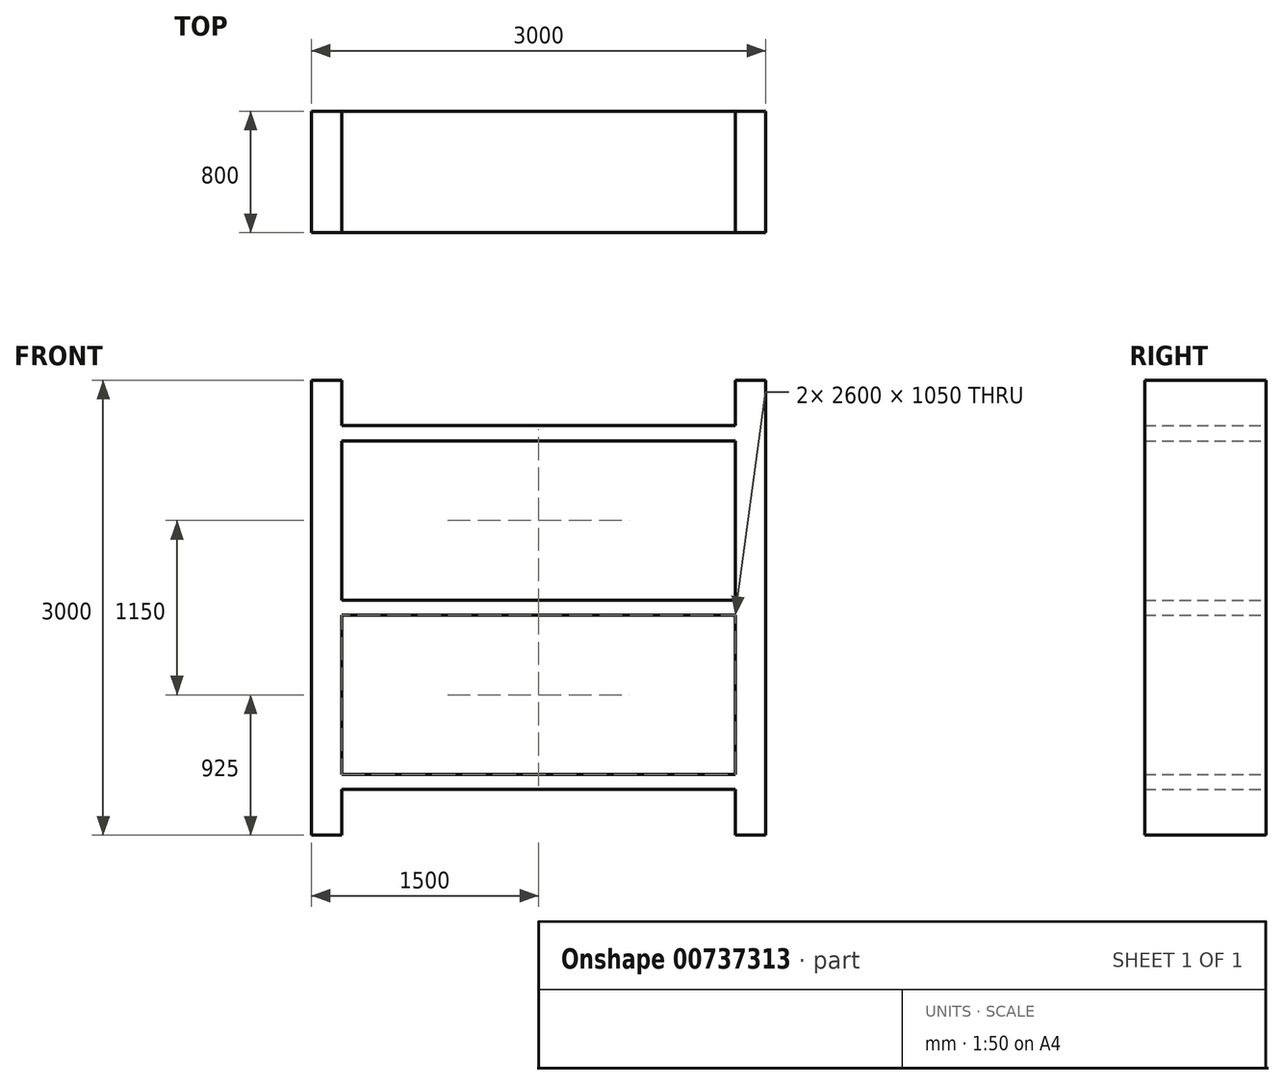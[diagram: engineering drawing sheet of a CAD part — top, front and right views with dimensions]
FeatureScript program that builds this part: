
annotation { "Feature Type Name" : "Feature", "Feature Type Description" : "" }
export const myFeature = defineFeature(function(context is Context, id is Id, definition is map)
    precondition{}
    {
        {
            var Q0;
            Q0=qCreatedBy(makeId("Front.planeOp"),FACE);
            var sketch = newSketch(context, id + "F0", { "sketchPlane" : qUnion([Q0])});
            skLineSegment(sketch, "E0", {"start": v(-2977.78, -1250) * mm, "end": v(-377.78, -1250) * mm});
            skLineSegment(sketch, "E1", {"start": v(-377.78, -1250) * mm, "end": v(-377.78, -1550) * mm});
            skLineSegment(sketch, "E2", {"start": v(-377.78, -1550) * mm, "end": v(-177.78, -1550) * mm});
            skLineSegment(sketch, "E3", {"start": v(-177.78, -1550) * mm, "end": v(-177.78, 1450) * mm});
            skLineSegment(sketch, "E4", {"start": v(-177.78, 1450) * mm, "end": v(-377.78, 1450) * mm});
            skLineSegment(sketch, "E5", {"start": v(-377.78, 1450) * mm, "end": v(-377.78, 1150) * mm});
            skLineSegment(sketch, "E6", {"start": v(-377.78, 1150) * mm, "end": v(-2977.78, 1150) * mm});
            skLineSegment(sketch, "E7", {"start": v(-2977.78, 1150) * mm, "end": v(-2977.78, 1450) * mm});
            skLineSegment(sketch, "E8", {"start": v(-2977.78, 1450) * mm, "end": v(-3177.78, 1450) * mm});
            skLineSegment(sketch, "E9", {"start": v(-2977.78, 1050) * mm, "end": v(-377.78, 1050) * mm});
            skLineSegment(sketch, "E10", {"start": v(-377.78, 1050) * mm, "end": v(-377.78, 0) * mm});
            skLineSegment(sketch, "E11", {"start": v(-377.78, 0) * mm, "end": v(-2977.78, 0) * mm});
            skLineSegment(sketch, "E12", {"start": v(-2977.78, -100) * mm, "end": v(-377.78, -100) * mm});
            skLineSegment(sketch, "E13", {"start": v(-377.78, -100) * mm, "end": v(-377.78, -1150) * mm});
            skLineSegment(sketch, "E14", {"start": v(-377.78, -1150) * mm, "end": v(-2977.78, -1150) * mm});
            skLineSegment(sketch, "E15", {"start": v(-2977.78, -1250) * mm, "end": v(-2977.78, -1550) * mm});
            skLineSegment(sketch, "E16", {"start": v(-2977.78, -1550) * mm, "end": v(-3177.78, -1550) * mm});
            skLineSegment(sketch, "E17", {"start": v(-2977.78, 1050) * mm, "end": v(-2977.78, 0) * mm});
            skLineSegment(sketch, "E18", {"start": v(-2977.78, -100) * mm, "end": v(-2977.78, -1150) * mm});
            skLineSegment(sketch, "E19", {"start": v(-3177.78, -1550) * mm, "end": v(-3177.78, 1450) * mm});
            skSolve(sketch);
        }
        {
            var Q0;
            Q0 = qSketchRegion(id + "F0", true);
            extrude(context, id + "F1", {"entities" : qUnion([Q0]), "depth" : 800 * mm, "offsetDistance" : 25 * mm});
        }
    });
